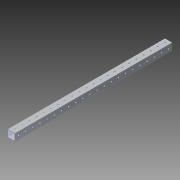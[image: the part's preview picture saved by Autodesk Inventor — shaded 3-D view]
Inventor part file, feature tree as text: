
AUTODESK INVENTOR PART (.ipt)
format: ipt  version: 2014 SP1 (Build 180222100, 222)  size: 1,276,416 bytes
history: native  units: in
note: dims shown in document units (in); Inventor stores cm internally (conversion verified against a paired STEP export)
features: pattern_circular x1, other x1, extrude x1, imported_body x1, sketch x1
ambient origin geometry x8: Origin, YZ Plane, XZ Plane, XY Plane, X Axis, Y Axis, Z Axis, Center Point
bodies: Body1 (feature_tree)
feature tree (5):
  pattern_circular  "CirPattern2"
  other  "1x1 tube1"
  extrude  "Extrusion1"  [1 undecoded]
  imported_body  "Base1"
  sketch  "Sketch1"  dims[d0=37.0in d1=0.0in]
note: 1 required parameter value undecoded (feature->parameter linkage not recoverable at this tier; creation-order binding heuristic only, values carry confidence <= 0.55)
